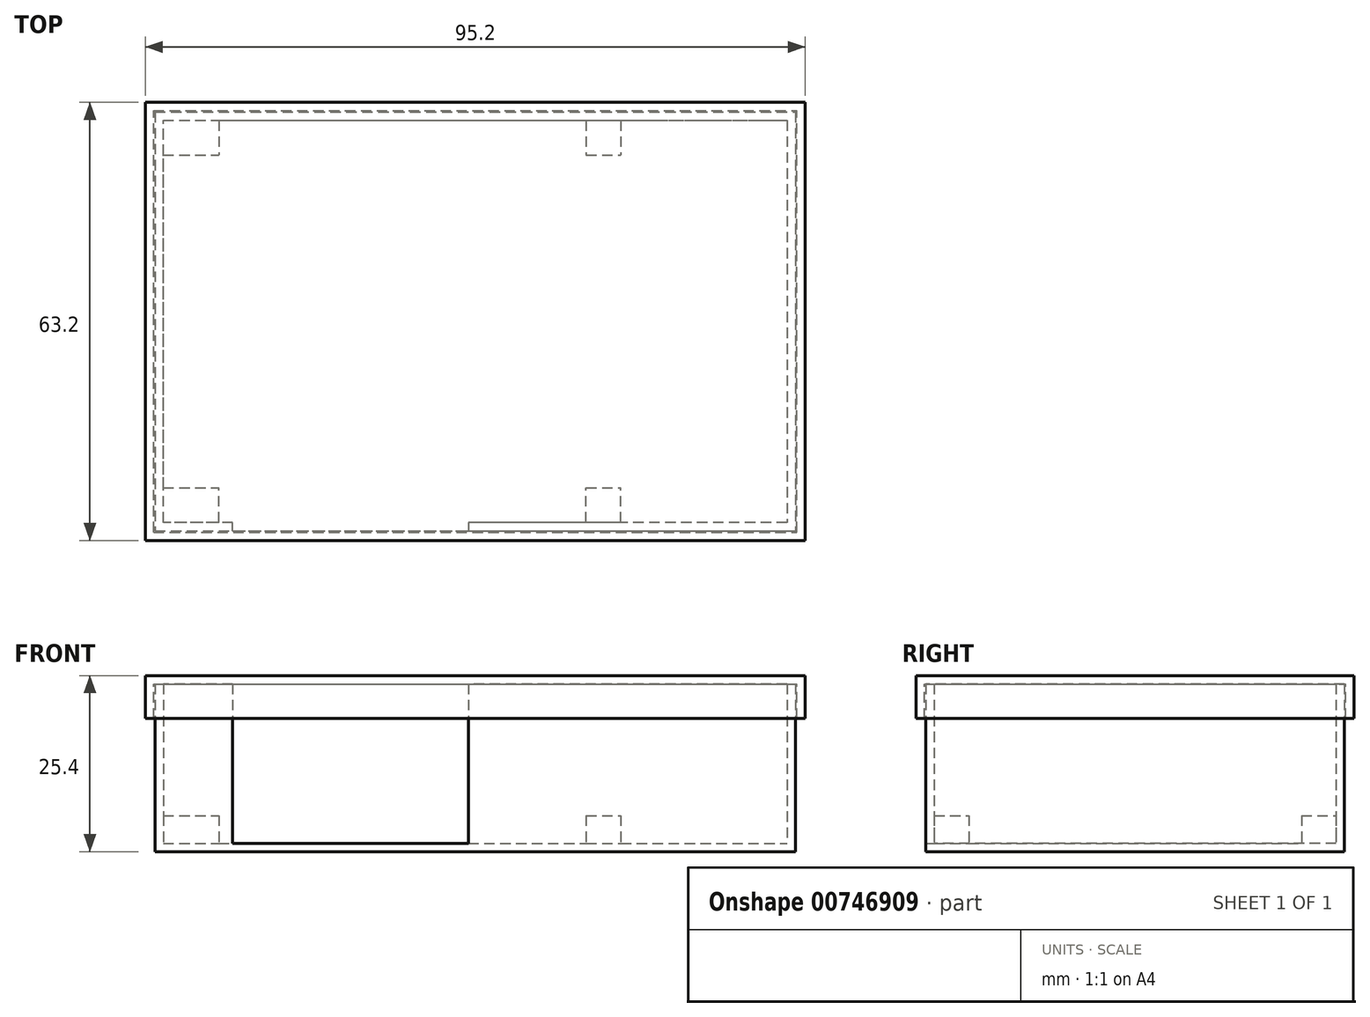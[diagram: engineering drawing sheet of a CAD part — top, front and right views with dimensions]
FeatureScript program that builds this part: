
annotation { "Feature Type Name" : "Feature", "Feature Type Description" : "" }
export const myFeature = defineFeature(function(context is Context, id is Id, definition is map)
    precondition{}
    {
        {
            var Q0;
            Q0=qCreatedBy(makeId("Top.planeOp"),FACE);
            var sketch = newSketch(context, id + "F0", { "sketchPlane" : qUnion([Q0])});
            skLineSegment(sketch, "E0.bottom", {"start": v(0, 0) * mm, "end": v(92.4, 0) * mm});
            skLineSegment(sketch, "E0.top", {"start": v(0, -60.4) * mm, "end": v(92.4, -60.4) * mm});
            skLineSegment(sketch, "E0.left", {"start": v(0, 0) * mm, "end": v(0, -60.4) * mm});
            skLineSegment(sketch, "E0.right", {"start": v(92.4, 0) * mm, "end": v(92.4, -60.4) * mm});
            skSolve(sketch);
        }
        {
            var Q0;
            Q0 = qSketchRegion(id + "F0", true);
            extrude(context, id + "F1", {"entities" : qUnion([Q0]), "depth" : 1.2 * mm, "offsetDistance" : 25 * mm});
        }
        {
            var Q0;
            Q0=makeQuery(id+"F1.opExtrude","CAP_FACE",FACE,{"disambiguationData":[OSD([sQuery(id+"F0.wireOp",EDGE,"E0.bottom"),sQuery(id+"F0.wireOp",EDGE,"E0.top"),sQuery(id+"F0.wireOp",EDGE,"E0.left"),sQuery(id+"F0.wireOp",EDGE,"E0.right")])],"isStart":false});
            var sketch = newSketch(context, id + "F2", { "sketchPlane" : qUnion([Q0])});
            skLineSegment(sketch, "E1", {"start": v(0, -60.4) * mm, "end": v(11.2, -60.4) * mm});
            skLineSegment(sketch, "E2", {"start": v(11.2, -60.4) * mm, "end": v(11.2, -59.2) * mm});
            skLineSegment(sketch, "E3", {"start": v(11.2, -59.2) * mm, "end": v(1.2, -59.2) * mm});
            skLineSegment(sketch, "E4", {"start": v(1.2, -59.2) * mm, "end": v(1.2, -1.2) * mm});
            skLineSegment(sketch, "E5", {"start": v(1.2, -1.2) * mm, "end": v(91.2, -1.2) * mm});
            skLineSegment(sketch, "E6", {"start": v(91.2, -1.2) * mm, "end": v(91.2, -59.2) * mm});
            skLineSegment(sketch, "E7", {"start": v(91.2, -59.2) * mm, "end": v(45.2, -59.2) * mm});
            skLineSegment(sketch, "E8", {"start": v(45.2, -59.2) * mm, "end": v(45.2, -60.4) * mm});
            skLineSegment(sketch, "E9", {"start": v(45.2, -60.4) * mm, "end": v(92.4, -60.4) * mm});
            skLineSegment(sketch, "E10", {"start": v(92.4, -60.4) * mm, "end": v(92.4, 0) * mm});
            skLineSegment(sketch, "E11", {"start": v(92.4, 0) * mm, "end": v(0, 0) * mm});
            skLineSegment(sketch, "E12", {"start": v(0, 0) * mm, "end": v(0, -60.4) * mm});
            skSolve(sketch);
        }
        {
            var Q0;
            Q0 = qSketchRegion(id + "F2", true);
            extrude(context, id + "F3", {"entities" : qUnion([Q0]), "operationType" : NewBodyOperationType.ADD, "depth" : 23 * mm, "offsetDistance" : 25 * mm});
        }
        {
            var Q0;
            Q0=makeQuery(id+"F1.opExtrude","CAP_FACE",FACE,{"disambiguationData":[OSD([sQuery(id+"F0.wireOp",EDGE,"E0.bottom"),sQuery(id+"F0.wireOp",EDGE,"E0.top"),sQuery(id+"F0.wireOp",EDGE,"E0.left"),sQuery(id+"F0.wireOp",EDGE,"E0.right")])],"isStart":false});
            var sketch = newSketch(context, id + "F4", { "sketchPlane" : qUnion([Q0])});
            skLineSegment(sketch, "E13.bottom", {"start": v(1.2, -1.2) * mm, "end": v(9.2, -1.2) * mm});
            skLineSegment(sketch, "E13.top", {"start": v(1.2, -6.2) * mm, "end": v(9.2, -6.2) * mm});
            skLineSegment(sketch, "E13.left", {"start": v(1.2, -1.2) * mm, "end": v(1.2, -6.2) * mm});
            skLineSegment(sketch, "E13.right", {"start": v(9.2, -1.2) * mm, "end": v(9.2, -6.2) * mm});
            skLineSegment(sketch, "E14.bottom", {"start": v(1.2, -59.2) * mm, "end": v(9.2, -59.2) * mm});
            skLineSegment(sketch, "E14.top", {"start": v(1.2, -54.2) * mm, "end": v(9.2, -54.2) * mm});
            skLineSegment(sketch, "E14.left", {"start": v(1.2, -59.2) * mm, "end": v(1.2, -54.2) * mm});
            skLineSegment(sketch, "E14.right", {"start": v(9.2, -59.2) * mm, "end": v(9.2, -54.2) * mm});
            skLineSegment(sketch, "E15.bottom", {"start": v(62.2, -59.2) * mm, "end": v(67.2, -59.2) * mm});
            skLineSegment(sketch, "E15.top", {"start": v(62.2, -54.2) * mm, "end": v(67.2, -54.2) * mm});
            skLineSegment(sketch, "E15.left", {"start": v(62.2, -59.2) * mm, "end": v(62.2, -54.2) * mm});
            skLineSegment(sketch, "E15.right", {"start": v(67.2, -59.2) * mm, "end": v(67.2, -54.2) * mm});
            skLineSegment(sketch, "E16.bottom", {"start": v(62.2, -1.2) * mm, "end": v(67.2, -1.2) * mm});
            skLineSegment(sketch, "E16.top", {"start": v(62.2, -6.2) * mm, "end": v(67.2, -6.2) * mm});
            skLineSegment(sketch, "E16.left", {"start": v(62.2, -1.2) * mm, "end": v(62.2, -6.2) * mm});
            skLineSegment(sketch, "E16.right", {"start": v(67.2, -1.2) * mm, "end": v(67.2, -6.2) * mm});
            skSolve(sketch);
        }
        {
            var Q0;
            Q0 = qSketchRegion(id + "F4", true);
            extrude(context, id + "F5", {"entities" : qUnion([Q0]), "operationType" : NewBodyOperationType.ADD, "depth" : 4 * mm, "offsetDistance" : 25 * mm});
        }
        {
            var Q0;
            Q0=makeQuery(id+"F3.opExtrude","CAP_FACE",FACE,{"disambiguationData":[OSD([sQuery(id+"F2.wireOp",EDGE,"E1"),sQuery(id+"F2.wireOp",EDGE,"E2"),sQuery(id+"F2.wireOp",EDGE,"E3"),sQuery(id+"F2.wireOp",EDGE,"E4"),sQuery(id+"F2.wireOp",EDGE,"E5"),sQuery(id+"F2.wireOp",EDGE,"E6"),sQuery(id+"F2.wireOp",EDGE,"E7"),sQuery(id+"F2.wireOp",EDGE,"E8"),sQuery(id+"F2.wireOp",EDGE,"E9"),sQuery(id+"F2.wireOp",EDGE,"E10"),sQuery(id+"F2.wireOp",EDGE,"E11"),sQuery(id+"F2.wireOp",EDGE,"E12")])],"isStart":false});
            var sketch = newSketch(context, id + "F6", { "sketchPlane" : qUnion([Q0])});
            skLineSegment(sketch, "E17.bottom", {"start": v(-1.4, 1.4) * mm, "end": v(93.8, 1.4) * mm});
            skLineSegment(sketch, "E17.top", {"start": v(-1.4, -61.8) * mm, "end": v(93.8, -61.8) * mm});
            skLineSegment(sketch, "E17.left", {"start": v(-1.4, 1.4) * mm, "end": v(-1.4, -61.8) * mm});
            skLineSegment(sketch, "E17.right", {"start": v(93.8, 1.4) * mm, "end": v(93.8, -61.8) * mm});
            skSolve(sketch);
        }
        {
            var Q0;
            Q0 = qSketchRegion(id + "F6", true);
            extrude(context, id + "F7", {"entities" : qUnion([Q0]), "depth" : 1.2 * mm, "offsetDistance" : 25 * mm});
        }
        {
            var Q0;
            Q0=makeQuery(id+"F7.opExtrude","CAP_FACE",FACE,{"disambiguationData":[OSD([sQuery(id+"F6.wireOp",EDGE,"E17.bottom"),sQuery(id+"F6.wireOp",EDGE,"E17.top"),sQuery(id+"F6.wireOp",EDGE,"E17.left"),sQuery(id+"F6.wireOp",EDGE,"E17.right")])],"isStart":true});
            var sketch = newSketch(context, id + "F8", { "sketchPlane" : qUnion([Q0])});
            skLineSegment(sketch, "E18.bottom", {"start": v(-1.4, 61.8) * mm, "end": v(93.8, 61.8) * mm});
            skLineSegment(sketch, "E18.top", {"start": v(-1.4, -1.4) * mm, "end": v(93.8, -1.4) * mm});
            skLineSegment(sketch, "E18.left", {"start": v(-1.4, 61.8) * mm, "end": v(-1.4, -1.4) * mm});
            skLineSegment(sketch, "E18.right", {"start": v(93.8, 61.8) * mm, "end": v(93.8, -1.4) * mm});
            skLineSegment(sketch, "E19.0", {"start": v(-0.2, -0.2) * mm, "end": v(92.6, -0.2) * mm});
            skLineSegment(sketch, "E19.1", {"start": v(-0.2, 60.6) * mm, "end": v(-0.2, -0.2) * mm});
            skLineSegment(sketch, "E19.2", {"start": v(-0.2, 60.6) * mm, "end": v(92.6, 60.6) * mm});
            skLineSegment(sketch, "E19.3", {"start": v(92.6, 60.6) * mm, "end": v(92.6, -0.2) * mm});
            skSolve(sketch);
        }
        {
            var Q0;
            Q0 = qSketchRegion(id + "F8", true);
            extrude(context, id + "F9", {"entities" : qUnion([Q0]), "operationType" : NewBodyOperationType.ADD, "depth" : 5 * mm, "offsetDistance" : 25 * mm});
        }
    });
